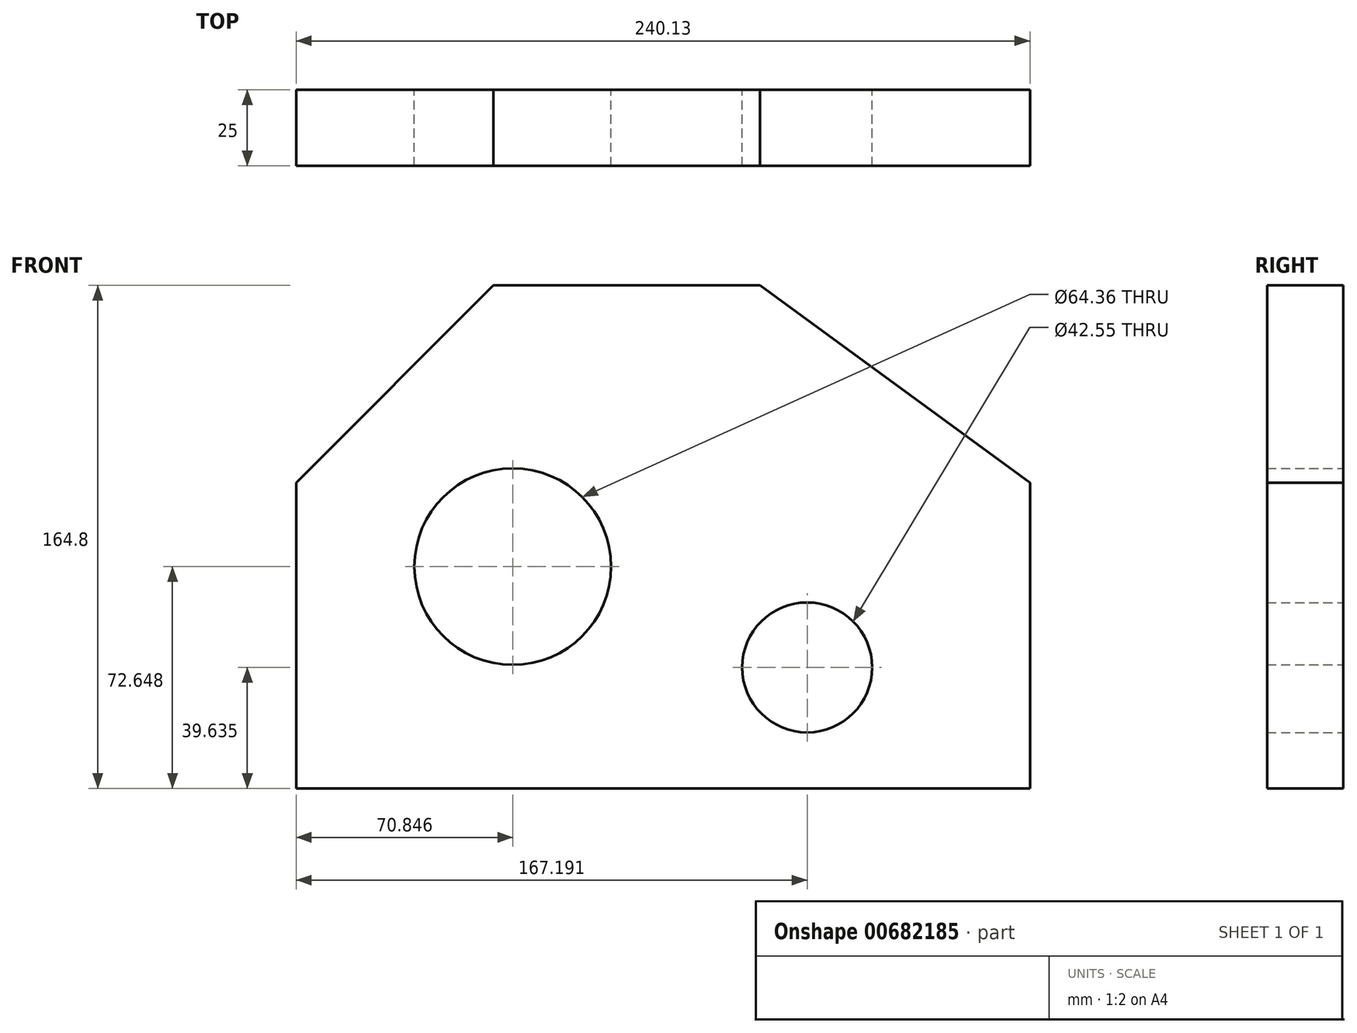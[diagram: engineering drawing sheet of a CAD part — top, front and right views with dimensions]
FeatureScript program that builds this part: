
annotation { "Feature Type Name" : "Feature", "Feature Type Description" : "" }
export const myFeature = defineFeature(function(context is Context, id is Id, definition is map)
    precondition{}
    {
        {
            var Q0;
            Q0=qCreatedBy(makeId("Front.planeOp"),FACE);
            var sketch = newSketch(context, id + "F0", { "sketchPlane" : qUnion([Q0])});
            skLineSegment(sketch, "E0", {"start": v(-76.41, 0) * mm, "end": v(163.72, 0) * mm});
            skLineSegment(sketch, "E1", {"start": v(-76.41, 0) * mm, "end": v(-76.41, 100.13) * mm});
            skLineSegment(sketch, "E2", {"start": v(-11.84, 164.8) * mm, "end": v(-76.41, 100.13) * mm});
            skLineSegment(sketch, "E3", {"start": v(-11.84, 164.8) * mm, "end": v(75.4, 164.8) * mm});
            skLineSegment(sketch, "E4", {"start": v(163.72, 0) * mm, "end": v(163.72, 100.13) * mm});
            skLineSegment(sketch, "E5", {"start": v(163.72, 100.13) * mm, "end": v(75.4, 164.8) * mm});
            skCircle(sketch, "E6", {"center": v(-5.56, 72.65) * mm, "radius": 32.18 * mm});
            skCircle(sketch, "E7", {"center": v(90.78, 39.63) * mm, "radius": 21.27 * mm});
            skSolve(sketch);
        }
        {
            var Q0;
            Q0 = qSketchRegion(id + "F0", true);
            extrude(context, id + "F1", {"entities" : qUnion([Q0]), "depth" : 25 * mm, "offsetDistance" : 25 * mm});
        }
    });
